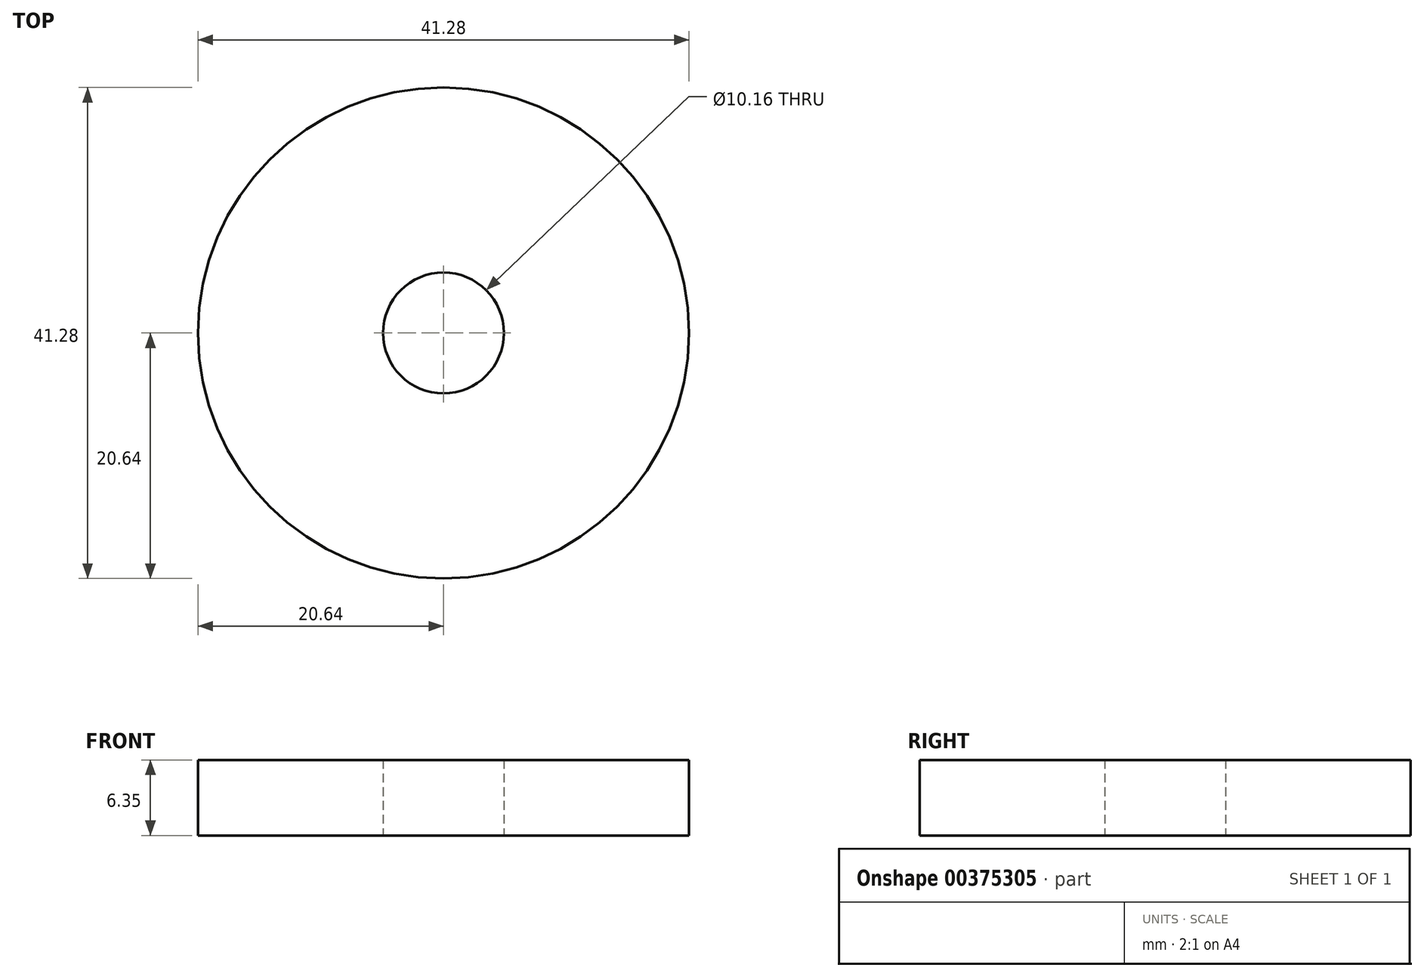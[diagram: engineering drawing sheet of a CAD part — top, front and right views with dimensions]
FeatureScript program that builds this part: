
annotation { "Feature Type Name" : "Feature", "Feature Type Description" : "" }
export const myFeature = defineFeature(function(context is Context, id is Id, definition is map)
    precondition{}
    {
        {
            var Q0;
            Q0=qCreatedBy(makeId("Top.planeOp"),FACE);
            var sketch = newSketch(context, id + "F0", { "sketchPlane" : qUnion([Q0])});
            skCircle(sketch, "E0", {"center": v(0, 0) * mm, "radius": 20.64 * mm});
            skCircle(sketch, "E1", {"center": v(0, 0) * mm, "radius": 5.08 * mm});
            skSolve(sketch);
        }
        {
            var Q0;
            Q0=makeQuery(id+"F0.imprint","IMPRINT",FACE,{"disambiguationData":[TD([[makeQuery(id+"F0.imprint","IMPRINT",EDGE,{"derivedFrom":sQuery(id+"F0.wireOp",EDGE,"E0")}),1.0]])]});
            extrude(context, id + "F1", {"entities" : qUnion([Q0]), "depth" : 6.35 * mm, "offsetDistance" : 25.4 * mm});
        }
    });
